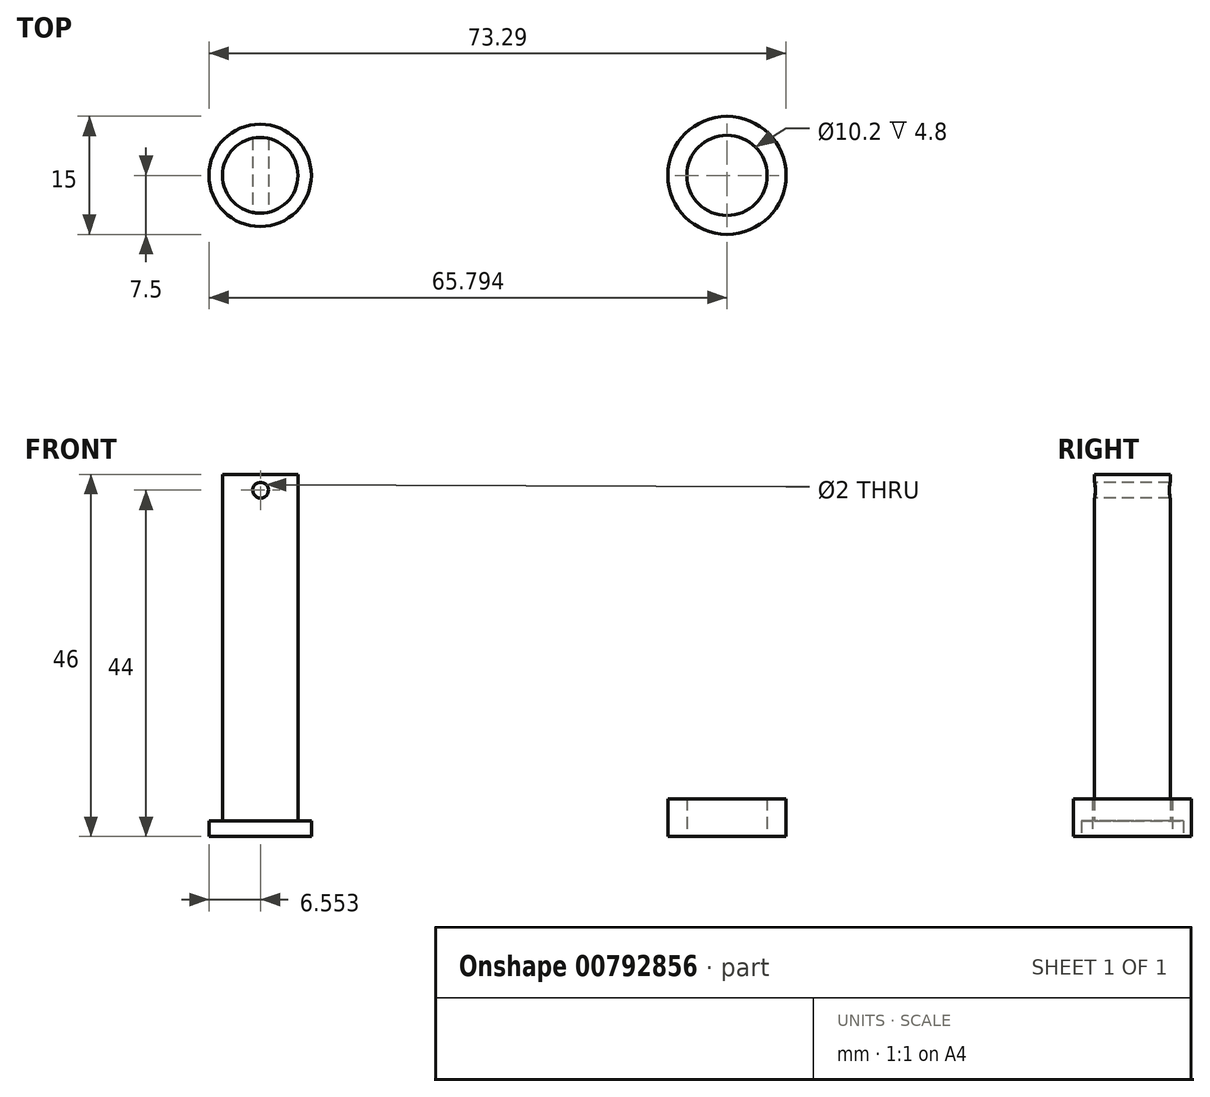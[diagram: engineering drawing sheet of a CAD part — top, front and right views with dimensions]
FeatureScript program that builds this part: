
annotation { "Feature Type Name" : "Feature", "Feature Type Description" : "" }
export const myFeature = defineFeature(function(context is Context, id is Id, definition is map)
    precondition{}
    {
        {
            var Q0;
            Q0=qCreatedBy(makeId("Top.planeOp"),FACE);
            var sketch = newSketch(context, id + "F0", { "sketchPlane" : qUnion([Q0])});
            skCircle(sketch, "E0", {"center": v(26.68, 0) * mm, "radius": 7.5 * mm});
            skCircle(sketch, "E1", {"center": v(26.68, 0) * mm, "radius": 5.1 * mm});
            skSolve(sketch);
        }
        {
            var Q0;
            Q0 = qSketchRegion(id + "F0", true);
            extrude(context, id + "F1", {"entities" : qUnion([Q0]), "depth" : 4.8 * mm, "offsetDistance" : 25 * mm});
        }
        {
            var Q0;
            Q0=qCreatedBy(makeId("Top.planeOp"),FACE);
            var sketch = newSketch(context, id + "F2", { "sketchPlane" : qUnion([Q0])});
            skCircle(sketch, "E2", {"center": v(-32.61, 0) * mm, "radius": 6.5 * mm});
            skSolve(sketch);
        }
        {
            var Q0;
            Q0 = qSketchRegion(id + "F2", true);
            extrude(context, id + "F3", {"entities" : qUnion([Q0]), "depth" : 2 * mm, "offsetDistance" : 25 * mm});
        }
        {
            var Q0;
            Q0=makeQuery(id+"F3.opExtrude","CAP_FACE",FACE,{"disambiguationData":[OSD([sQuery(id+"F2.wireOp",EDGE,"E2")])],"isStart":false});
            var sketch = newSketch(context, id + "F4", { "sketchPlane" : qUnion([Q0])});
            skCircle(sketch, "E3", {"center": v(-32.61, 0) * mm, "radius": 4.8 * mm});
            skSolve(sketch);
        }
        {
            var Q0;
            Q0 = qSketchRegion(id + "F4", true);
            extrude(context, id + "F5", {"entities" : qUnion([Q0]), "operationType" : NewBodyOperationType.ADD, "depth" : 44 * mm, "offsetDistance" : 25 * mm});
        }
        {
            var Q0;
            Q0=qCreatedBy(makeId("Front.planeOp"),FACE);
            cPlane(context, id + "F6", {"entities" : qUnion([Q0]), "cplaneType" : CPlaneType.OFFSET, "offset" : 10 * mm, "width" : 150 * mm, "height" : 150 * mm});
        }
        {
            var Q0;
            Q0=qCreatedBy(id+"F6.planeOp",FACE);
            var sketch = newSketch(context, id + "F7", { "sketchPlane" : qUnion([Q0])});
            skCircle(sketch, "E4", {"center": v(-32.56, 44) * mm, "radius": 1 * mm});
            skLineSegment(sketch, "E5", {"start": v(-55.81, 44) * mm, "end": v(-11, 44) * mm, "construction": true});
            skLineSegment(sketch, "E6", {"start": v(-55.6, 46) * mm, "end": v(-11, 46) * mm, "construction": true});
            skLineSegment(sketch, "E7", {"start": v(-55.39, 0) * mm, "end": v(-14.59, 0) * mm, "construction": true});
            skSolve(sketch);
        }
        {
            var Q0;
            Q0 = qSketchRegion(id + "F7", true);
            extrude(context, id + "F8", {"entities" : qUnion([Q0]), "operationType" : NewBodyOperationType.REMOVE, "oppositeDirection" : true, "depth" : 63 * mm, "offsetDistance" : 25 * mm});
        }
    });
